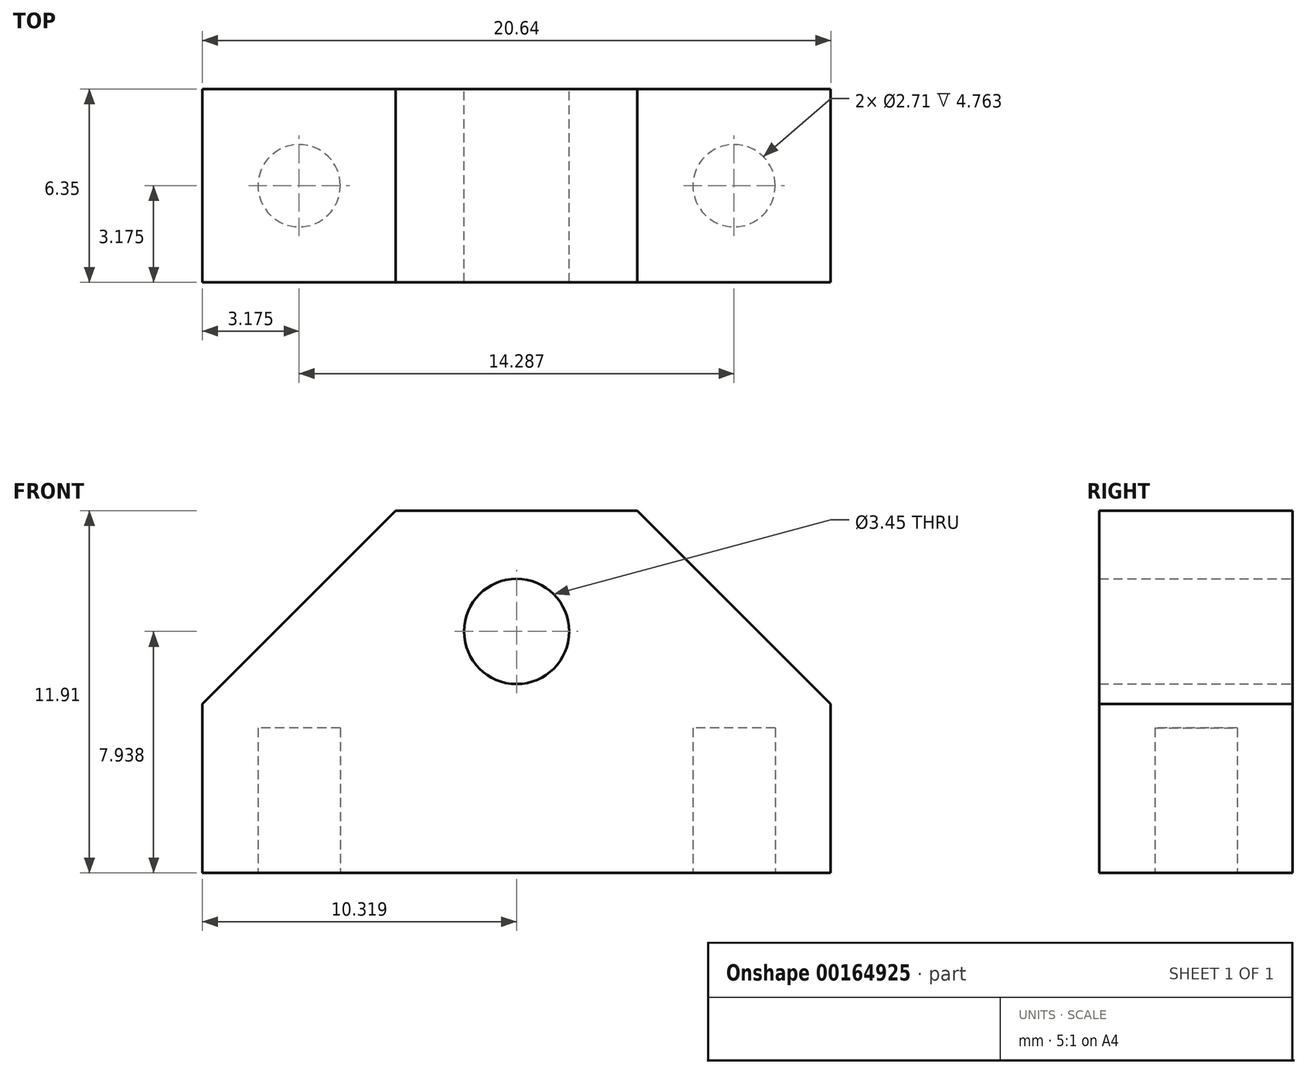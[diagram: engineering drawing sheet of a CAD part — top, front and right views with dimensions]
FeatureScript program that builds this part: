
annotation { "Feature Type Name" : "Feature", "Feature Type Description" : "" }
export const myFeature = defineFeature(function(context is Context, id is Id, definition is map)
    precondition{}
    {
        {
            var Q0;
            Q0=qCreatedBy(makeId("Top.planeOp"),FACE);
            var sketch = newSketch(context, id + "F0", { "sketchPlane" : qUnion([Q0])});
            skLineSegment(sketch, "E0.bottom", {"start": v(0, 0) * mm, "end": v(20.64, 0) * mm});
            skLineSegment(sketch, "E0.top", {"start": v(0, 6.35) * mm, "end": v(20.64, 6.35) * mm});
            skLineSegment(sketch, "E0.left", {"start": v(0, 0) * mm, "end": v(0, 6.35) * mm});
            skLineSegment(sketch, "E0.right", {"start": v(20.64, 0) * mm, "end": v(20.64, 6.35) * mm});
            skLineSegment(sketch, "E1", {"start": v(0, 3.17) * mm, "end": v(3.17, 3.17) * mm, "construction": true});
            skLineSegment(sketch, "E2", {"start": v(3.17, 3.17) * mm, "end": v(3.17, 0) * mm, "construction": true});
            skLineSegment(sketch, "E3", {"start": v(20.64, 3.18) * mm, "end": v(17.46, 3.18) * mm, "construction": true});
            skCircle(sketch, "E4", {"center": v(3.17, 3.17) * mm, "radius": 1.35 * mm});
            skCircle(sketch, "E5", {"center": v(17.46, 3.18) * mm, "radius": 1.35 * mm});
            skSolve(sketch);
        }
        {
            var Q0;
            Q0 = qSketchRegion(id + "F0", true);
            extrude(context, id + "F1", {"entities" : qUnion([Q0]), "depth" : 4.76 * mm});
        }
        {
            var Q0;
            Q0=makeQuery(id+"F1.opExtrude","CAP_FACE",FACE,{"disambiguationData":[OSD([sQuery(id+"F0.wireOp",EDGE,"E0.bottom"),sQuery(id+"F0.wireOp",EDGE,"E0.top"),sQuery(id+"F0.wireOp",EDGE,"E0.left"),sQuery(id+"F0.wireOp",EDGE,"E0.right"),sQuery(id+"F0.wireOp",EDGE,"E4"),sQuery(id+"F0.wireOp",EDGE,"E5")])],"isStart":false});
            var sketch = newSketch(context, id + "F2", { "sketchPlane" : qUnion([Q0])});
            skLineSegment(sketch, "E6.bottom", {"start": v(20.64, 0) * mm, "end": v(0, 0) * mm});
            skLineSegment(sketch, "E6.top", {"start": v(20.64, 6.35) * mm, "end": v(0, 6.35) * mm});
            skLineSegment(sketch, "E6.left", {"start": v(20.64, 0) * mm, "end": v(20.64, 6.35) * mm});
            skLineSegment(sketch, "E6.right", {"start": v(0, 0) * mm, "end": v(0, 6.35) * mm});
            skSolve(sketch);
        }
        {
            var Q0;
            Q0 = qSketchRegion(id + "F2", true);
            extrude(context, id + "F3", {"entities" : qUnion([Q0]), "operationType" : NewBodyOperationType.ADD, "depth" : 7.14 * mm});
        }
        {
            var Q0;
            Q0=makeQuery(id+"F3.opExtrude","CAP_EDGE",EDGE,{"disambiguationData":[OSD([sQuery(id+"F2.wireOp",EDGE,"E6.left")])],"isStart":false});
            var Q1;
            Q1=makeQuery(id+"F3.opExtrude","CAP_EDGE",EDGE,{"disambiguationData":[OSD([sQuery(id+"F2.wireOp",EDGE,"E6.right")])],"isStart":false});
            chamfer(context, id + "F4", {"entities" : qUnion([Q0, Q1]), "width" : 6.35 * mm, "tangentPropagation" : true});
        }
        {
            var Q0;
            Q0=makeQuery(id+"F3.boolean.opBoolean","MERGE",FACE,{"derivedFrom":[makeQuery(id+"F1.opExtrude","SWEPT_FACE",FACE,{"disambiguationData":[OSD([sQuery(id+"F0.wireOp",EDGE,"E0.top")])]}),makeQuery(id+"F3.opExtrude","SWEPT_FACE",FACE,{"disambiguationData":[OSD([sQuery(id+"F2.wireOp",EDGE,"E6.top")])]})]});
            var sketch = newSketch(context, id + "F5", { "sketchPlane" : qUnion([Q0])});
            skLineSegment(sketch, "E7.bottom", {"start": v(-6.35, 11.9) * mm, "end": v(-10.32, 11.9) * mm, "construction": true});
            skLineSegment(sketch, "E7.top", {"start": v(-6.35, 7.94) * mm, "end": v(-10.32, 7.94) * mm, "construction": true});
            skLineSegment(sketch, "E7.left", {"start": v(-6.35, 11.9) * mm, "end": v(-6.35, 7.94) * mm, "construction": true});
            skLineSegment(sketch, "E7.right", {"start": v(-10.32, 11.9) * mm, "end": v(-10.32, 7.94) * mm, "construction": true});
            skCircle(sketch, "E8", {"center": v(-10.32, 7.94) * mm, "radius": 1.73 * mm});
            skSolve(sketch);
        }
        {
            var Q0;
            Q0 = qSketchRegion(id + "F5", true);
            var Q1;
            Q1=makeQuery(id+"F3.boolean.opBoolean","MERGE",FACE,{"derivedFrom":[makeQuery(id+"F1.opExtrude","SWEPT_FACE",FACE,{"disambiguationData":[OSD([sQuery(id+"F0.wireOp",EDGE,"E0.bottom")])]}),makeQuery(id+"F3.opExtrude","SWEPT_FACE",FACE,{"disambiguationData":[OSD([sQuery(id+"F2.wireOp",EDGE,"E6.bottom")])]})]});
            extrude(context, id + "F6", {"entities" : qUnion([Q0]), "operationType" : NewBodyOperationType.REMOVE, "endBound" : BoundingType.UP_TO_SURFACE, "oppositeDirection" : true, "endBoundEntityFace" : qUnion([Q1]), "depth" : 25.4 * mm});
        }
    });
